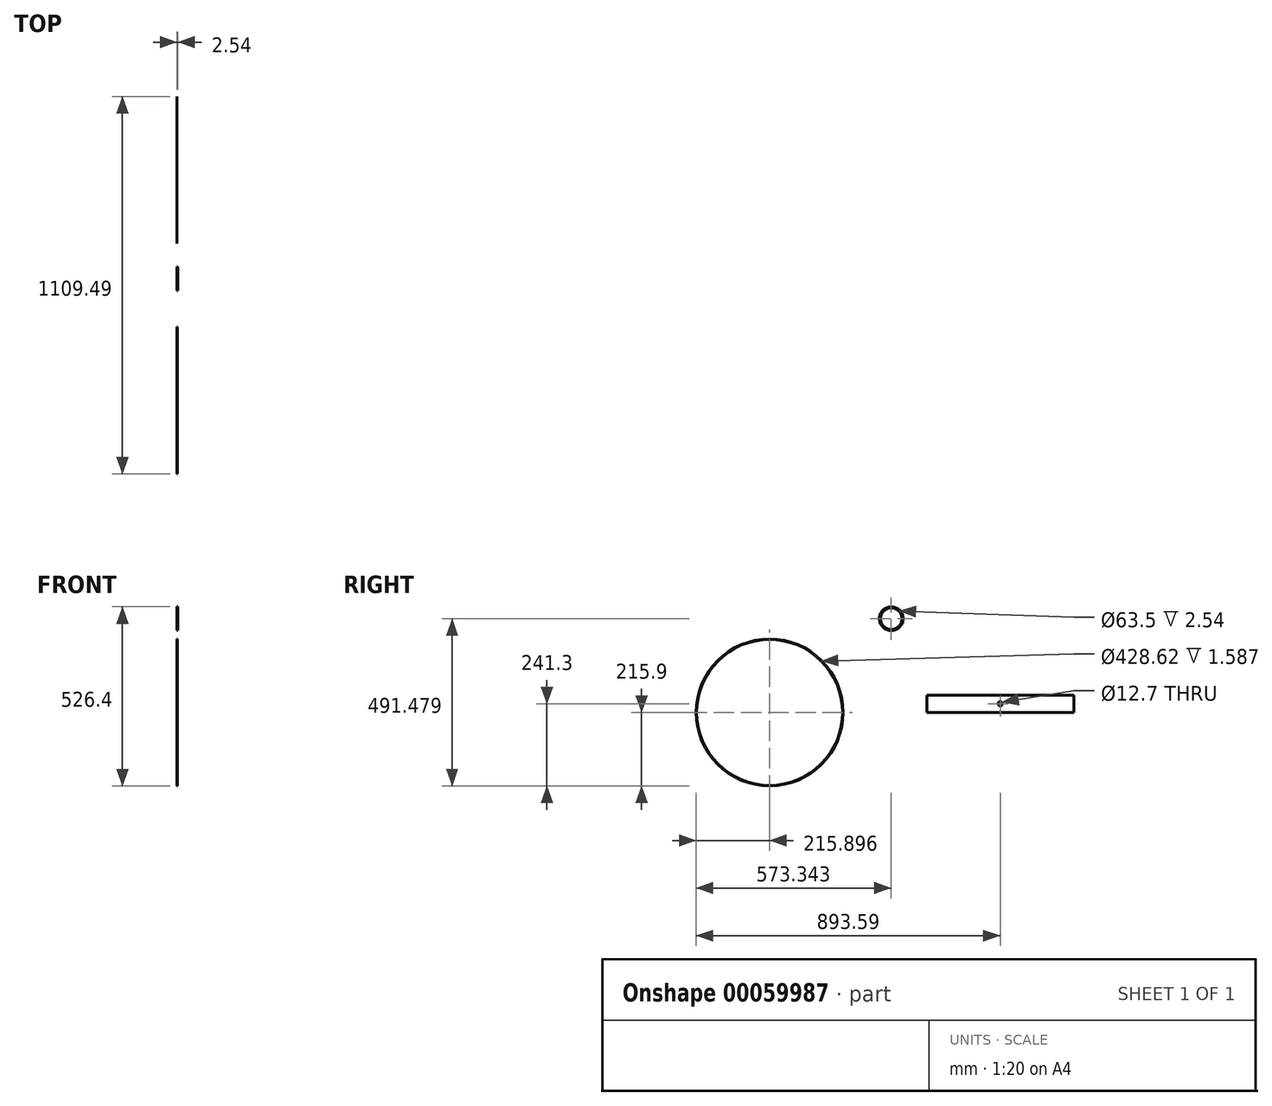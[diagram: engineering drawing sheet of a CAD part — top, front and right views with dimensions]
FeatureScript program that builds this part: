
annotation { "Feature Type Name" : "Feature", "Feature Type Description" : "" }
export const myFeature = defineFeature(function(context is Context, id is Id, definition is map)
    precondition{}
    {
        {
            var Q0;
            Q0=qCreatedBy(makeId("Right.planeOp"),FACE);
            var sketch = newSketch(context, id + "F0", { "sketchPlane" : qUnion([Q0])});
            skLineSegment(sketch, "E0.bottom", {"start": v(0, 0) * mm, "end": v(431.8, 0) * mm});
            skLineSegment(sketch, "E0.top", {"start": v(0, 50.8) * mm, "end": v(431.8, 50.8) * mm});
            skLineSegment(sketch, "E0.left", {"start": v(0, 0) * mm, "end": v(0, 50.8) * mm});
            skLineSegment(sketch, "E0.right", {"start": v(431.8, 0) * mm, "end": v(431.8, 50.8) * mm});
            skCircle(sketch, "E1", {"center": v(215.9, 25.4) * mm, "radius": 6.35 * mm});
            skPoint(sketch, "E1.centerSnap0", {"position": v(0, 25.4) * mm});
            skPoint(sketch, "E1.centerSnap1", {"position": v(215.9, 50.8) * mm});
            skSolve(sketch);
        }
        {
            var Q0;
            Q0=makeQuery(id+"F0.imprint","IMPRINT",FACE,{"disambiguationData":[TD([[makeQuery(id+"F0.imprint","IMPRINT",EDGE,{"derivedFrom":sQuery(id+"F0.wireOp",EDGE,"E0.bottom")}),1.0]])]});
            extrude(context, id + "F1", {"entities" : qUnion([Q0]), "depth" : 0.25 * mm});
        }
        {
            var Q0;
            Q0=qCreatedBy(makeId("Right.planeOp"),FACE);
            var sketch = newSketch(context, id + "F2", { "sketchPlane" : qUnion([Q0])});
            skCircle(sketch, "E2", {"center": v(-461.8, 0) * mm, "radius": 215.9 * mm});
            skCircle(sketch, "E3", {"center": v(-461.8, 0) * mm, "radius": 214.31 * mm});
            skSolve(sketch);
        }
        {
            var Q0;
            Q0=makeQuery(id+"F2.imprint","IMPRINT",FACE,{"disambiguationData":[TD([[makeQuery(id+"F2.imprint","IMPRINT",EDGE,{"derivedFrom":sQuery(id+"F2.wireOp",EDGE,"E2")}),1.0]])]});
            var Q1;
            Q1=makeQuery(id+"F2.imprint","IMPRINT",FACE,{"disambiguationData":[TD([[makeQuery(id+"F2.imprint","IMPRINT",EDGE,{"derivedFrom":sQuery(id+"F2.wireOp",EDGE,"5f7109d8-5ec9-4a36-8a0f-8295b10b4481")}),1.0]])]});
            extrude(context, id + "F3", {"entities" : qUnion([Q0, Q1]), "depth" : 1.59 * mm});
        }
        {
            var Q0;
            Q0=qCreatedBy(makeId("Right.planeOp"),FACE);
            var sketch = newSketch(context, id + "F4", { "sketchPlane" : qUnion([Q0])});
            skCircle(sketch, "E4", {"center": v(-104.35, 275.58) * mm, "radius": 34.93 * mm});
            skCircle(sketch, "E5", {"center": v(-104.35, 275.58) * mm, "radius": 31.75 * mm});
            skSolve(sketch);
        }
        {
            var Q0;
            Q0=makeQuery(id+"F4.imprint","IMPRINT",FACE,{"disambiguationData":[TD([[makeQuery(id+"F4.imprint","IMPRINT",EDGE,{"derivedFrom":sQuery(id+"F4.wireOp",EDGE,"E4")}),1.0]])]});
            extrude(context, id + "F5", {"entities" : qUnion([Q0]), "depth" : 2.54 * mm});
        }
    });
